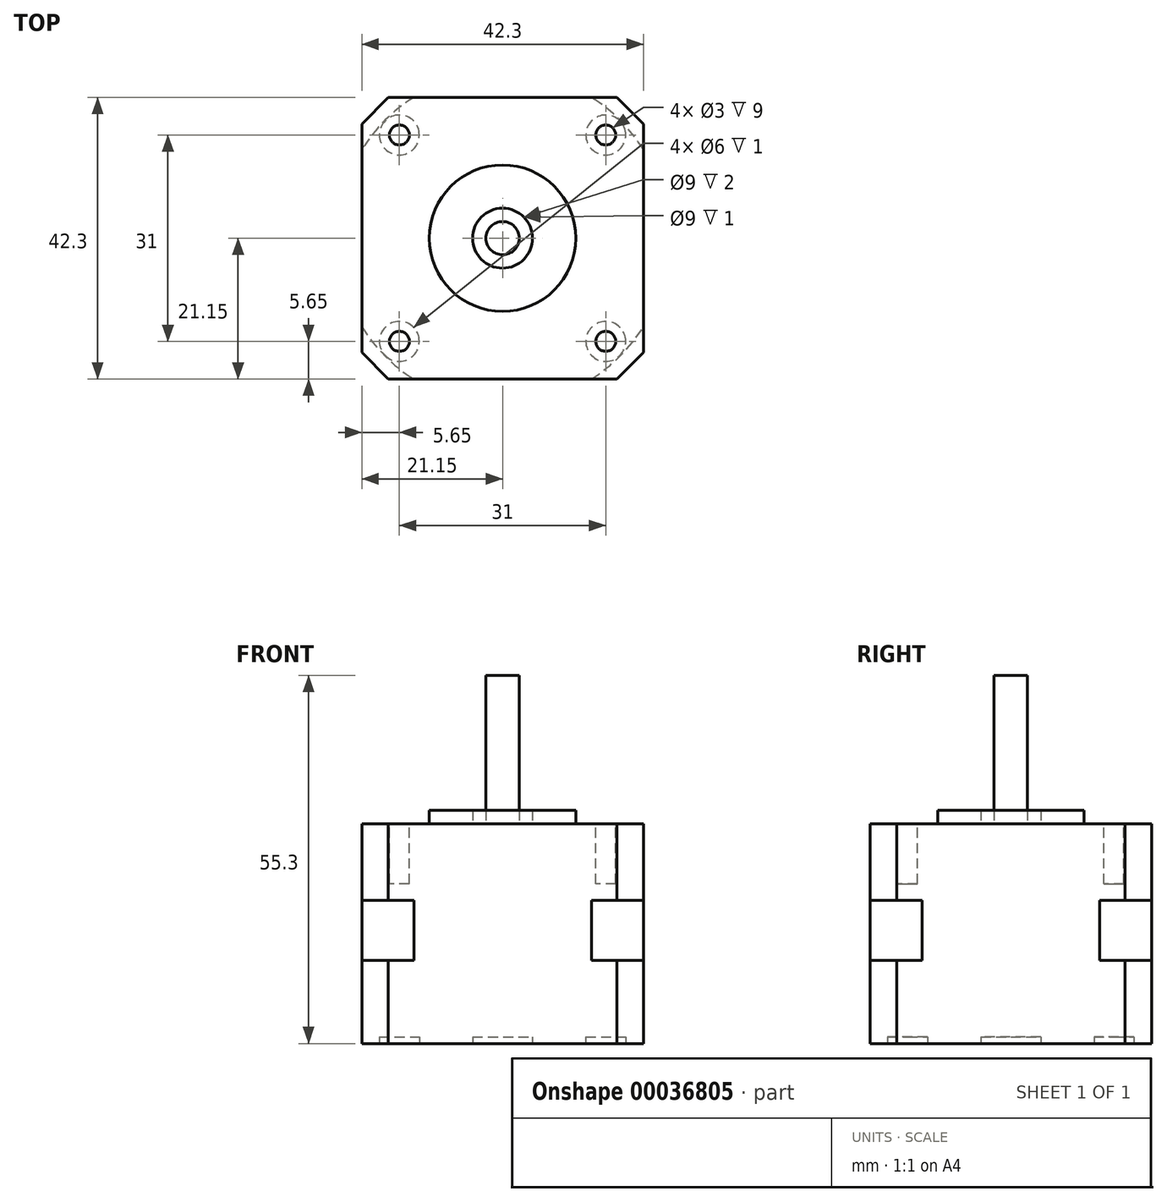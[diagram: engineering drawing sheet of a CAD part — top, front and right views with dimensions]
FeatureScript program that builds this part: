
annotation { "Feature Type Name" : "Feature", "Feature Type Description" : "" }
export const myFeature = defineFeature(function(context is Context, id is Id, definition is map)
    precondition{}
    {
        {
            var Q0;
            Q0=qCreatedBy(makeId("Top.planeOp"),FACE);
            var sketch = newSketch(context, id + "F0", { "sketchPlane" : qUnion([Q0])});
            skLineSegment(sketch, "E0.rect.bottom", {"start": v(-21.15, 21.15) * mm, "end": v(21.15, 21.15) * mm});
            skLineSegment(sketch, "E0.rect.top", {"start": v(-21.15, -21.15) * mm, "end": v(21.15, -21.15) * mm});
            skLineSegment(sketch, "E0.rect.left", {"start": v(-21.15, 21.15) * mm, "end": v(-21.15, -21.15) * mm});
            skLineSegment(sketch, "E0.rect.right", {"start": v(21.15, 21.15) * mm, "end": v(21.15, -21.15) * mm});
            skPoint(sketch, "E0.rect.middle", {"position": v(0, 0) * mm});
            skSolve(sketch);
        }
        {
            var Q0;
            Q0 = qSketchRegion(id + "F0", true);
            extrude(context, id + "F1", {"entities" : qUnion([Q0]), "depth" : 33 * mm});
        }
        {
            var Q0;
            Q0=makeQuery(id+"F1.opExtrude","SWEPT_EDGE",EDGE,{"disambiguationData":[OSD([sQuery(id+"F0.wireOp",EDGE,"E0.rect.top"),sQuery(id+"F0.wireOp",EDGE,"E0.rect.right")])]});
            var Q1;
            Q1=makeQuery(id+"F1.opExtrude","SWEPT_EDGE",EDGE,{"disambiguationData":[OSD([sQuery(id+"F0.wireOp",EDGE,"E0.rect.top"),sQuery(id+"F0.wireOp",EDGE,"E0.rect.left")])]});
            var Q2;
            Q2=makeQuery(id+"F1.opExtrude","SWEPT_EDGE",EDGE,{"disambiguationData":[OSD([sQuery(id+"F0.wireOp",EDGE,"E0.rect.bottom"),sQuery(id+"F0.wireOp",EDGE,"E0.rect.right")])]});
            var Q3;
            Q3=makeQuery(id+"F1.opExtrude","SWEPT_EDGE",EDGE,{"disambiguationData":[OSD([sQuery(id+"F0.wireOp",EDGE,"E0.rect.bottom"),sQuery(id+"F0.wireOp",EDGE,"E0.rect.left")])]});
            chamfer(context, id + "F2", {"entities" : qUnion([Q0, Q1, Q2, Q3]), "width" : 4 * mm, "tangentPropagation" : true});
        }
        {
            var Q0;
            Q0=makeQuery(id+"F1.opExtrude","CAP_FACE",FACE,{"disambiguationData":[OSD([sQuery(id+"F0.wireOp",EDGE,"E0.rect.bottom"),sQuery(id+"F0.wireOp",EDGE,"E0.rect.top"),sQuery(id+"F0.wireOp",EDGE,"E0.rect.left"),sQuery(id+"F0.wireOp",EDGE,"E0.rect.right")])],"isStart":false});
            var sketch = newSketch(context, id + "F3", { "sketchPlane" : qUnion([Q0])});
            skCircle(sketch, "E1", {"center": v(0, 0) * mm, "radius": 11 * mm});
            skCircle(sketch, "E2", {"center": v(0, 0) * mm, "radius": 4.5 * mm});
            skSolve(sketch);
        }
        {
            var Q0;
            Q0 = qSketchRegion(id + "F3", true);
            extrude(context, id + "F4", {"entities" : qUnion([Q0]), "operationType" : NewBodyOperationType.ADD, "depth" : 2 * mm});
        }
        {
            var Q0;
            Q0=makeQuery(id+"F1.opExtrude","CAP_FACE",FACE,{"disambiguationData":[OSD([sQuery(id+"F0.wireOp",EDGE,"E0.rect.bottom"),sQuery(id+"F0.wireOp",EDGE,"E0.rect.top"),sQuery(id+"F0.wireOp",EDGE,"E0.rect.left"),sQuery(id+"F0.wireOp",EDGE,"E0.rect.right")])],"isStart":false});
            var sketch = newSketch(context, id + "F5", { "sketchPlane" : qUnion([Q0])});
            skLineSegment(sketch, "E3.rect.bottom", {"start": v(15.5, 15.5) * mm, "end": v(-15.5, 15.5) * mm, "construction": true});
            skLineSegment(sketch, "E3.rect.top", {"start": v(15.5, -15.5) * mm, "end": v(-15.5, -15.5) * mm, "construction": true});
            skLineSegment(sketch, "E3.rect.left", {"start": v(15.5, 15.5) * mm, "end": v(15.5, -15.5) * mm, "construction": true});
            skLineSegment(sketch, "E3.rect.right", {"start": v(-15.5, 15.5) * mm, "end": v(-15.5, -15.5) * mm, "construction": true});
            skPoint(sketch, "E3.rect.middle", {"position": v(0, 0) * mm});
            skCircle(sketch, "E4", {"center": v(15.5, 15.5) * mm, "radius": 1.5 * mm});
            skCircle(sketch, "E5", {"center": v(15.5, -15.5) * mm, "radius": 1.5 * mm});
            skCircle(sketch, "E6", {"center": v(-15.5, -15.5) * mm, "radius": 1.5 * mm});
            skCircle(sketch, "E7", {"center": v(-15.5, 15.5) * mm, "radius": 1.5 * mm});
            skSolve(sketch);
        }
        {
            var Q0;
            Q0 = qSketchRegion(id + "F5", true);
            extrude(context, id + "F6", {"entities" : qUnion([Q0]), "operationType" : NewBodyOperationType.REMOVE, "oppositeDirection" : true, "depth" : 9 * mm});
        }
        {
            var Q0;
            Q0=makeQuery(id+"F1.opExtrude","CAP_FACE",FACE,{"disambiguationData":[OSD([sQuery(id+"F0.wireOp",EDGE,"E0.rect.bottom"),sQuery(id+"F0.wireOp",EDGE,"E0.rect.top"),sQuery(id+"F0.wireOp",EDGE,"E0.rect.left"),sQuery(id+"F0.wireOp",EDGE,"E0.rect.right")])],"isStart":true});
            var sketch = newSketch(context, id + "F7", { "sketchPlane" : qUnion([Q0])});
            skLineSegment(sketch, "E8.rect.bottom", {"start": v(-15.5, -15.5) * mm, "end": v(15.5, -15.5) * mm, "construction": true});
            skLineSegment(sketch, "E8.rect.top", {"start": v(-15.5, 15.5) * mm, "end": v(15.5, 15.5) * mm, "construction": true});
            skLineSegment(sketch, "E8.rect.left", {"start": v(-15.5, -15.5) * mm, "end": v(-15.5, 15.5) * mm, "construction": true});
            skLineSegment(sketch, "E8.rect.right", {"start": v(15.5, -15.5) * mm, "end": v(15.5, 15.5) * mm, "construction": true});
            skPoint(sketch, "E8.rect.middle", {"position": v(0, 0) * mm});
            skCircle(sketch, "E9", {"center": v(0, 0) * mm, "radius": 4.5 * mm});
            skCircle(sketch, "E10", {"center": v(-15.5, 15.5) * mm, "radius": 3 * mm});
            skCircle(sketch, "E11", {"center": v(-15.5, -15.5) * mm, "radius": 3 * mm});
            skCircle(sketch, "E12", {"center": v(15.5, -15.5) * mm, "radius": 3 * mm});
            skCircle(sketch, "E13", {"center": v(15.5, 15.5) * mm, "radius": 3 * mm});
            skSolve(sketch);
        }
        {
            var Q0;
            Q0 = qSketchRegion(id + "F7", true);
            extrude(context, id + "F8", {"entities" : qUnion([Q0]), "operationType" : NewBodyOperationType.REMOVE, "oppositeDirection" : true, "depth" : 1 * mm});
        }
        {
            var Q0;
            Q0=makeQuery(id+"F4.boolean.opBoolean","SPLIT",FACE,{"disambiguationData":[TD([makeQuery(id+"F4.opExtrude","SWEPT_FACE",FACE,{"disambiguationData":[OSD([sQuery(id+"F3.wireOp",EDGE,"E2")])]})])],"derivedFrom":makeQuery(id+"F1.opExtrude","CAP_FACE",FACE,{"disambiguationData":[OSD([sQuery(id+"F0.wireOp",EDGE,"E0.rect.bottom"),sQuery(id+"F0.wireOp",EDGE,"E0.rect.top"),sQuery(id+"F0.wireOp",EDGE,"E0.rect.left"),sQuery(id+"F0.wireOp",EDGE,"E0.rect.right")])],"isStart":false})});
            var sketch = newSketch(context, id + "F9", { "sketchPlane" : qUnion([Q0])});
            skCircle(sketch, "E14", {"center": v(0, 0) * mm, "radius": 2.5 * mm});
            skSolve(sketch);
        }
        {
            var Q0;
            Q0 = qSketchRegion(id + "F9", true);
            extrude(context, id + "F10", {"entities" : qUnion([Q0]), "operationType" : NewBodyOperationType.ADD, "depth" : 22.3 * mm});
        }
        {
            var Q0;
            Q0=qCreatedBy(makeId("Right.planeOp"),FACE);
            var sketch = newSketch(context, id + "F11", { "sketchPlane" : qUnion([Q0])});
            skLineSegment(sketch, "E15.bottom", {"start": v(31.27, 21.5) * mm, "end": v(25, 21.5) * mm});
            skLineSegment(sketch, "E15.top", {"start": v(31.27, 12.5) * mm, "end": v(25, 12.5) * mm});
            skLineSegment(sketch, "E15.left", {"start": v(31.27, 21.5) * mm, "end": v(31.27, 12.5) * mm});
            skLineSegment(sketch, "E15.right", {"start": v(25, 21.5) * mm, "end": v(25, 12.5) * mm});
            skLineSegment(sketch, "E16", {"start": v(0, 0) * mm, "end": v(0, 25.1) * mm, "construction": true});
            skSolve(sketch);
        }
        {
            var Q0;
            Q0 = qSketchRegion(id + "F11", true);
            var Q1;
            Q1=sQuery(id+"F11.wireOp",EDGE,"E16");
            revolve(context, id + "F12", {"operationType" : NewBodyOperationType.REMOVE, "entities" : qUnion([Q0]), "axis" : qUnion([Q1]), "revolveType" : RevolveType.FULL, "oppositeDirection" : true});
        }
    });
